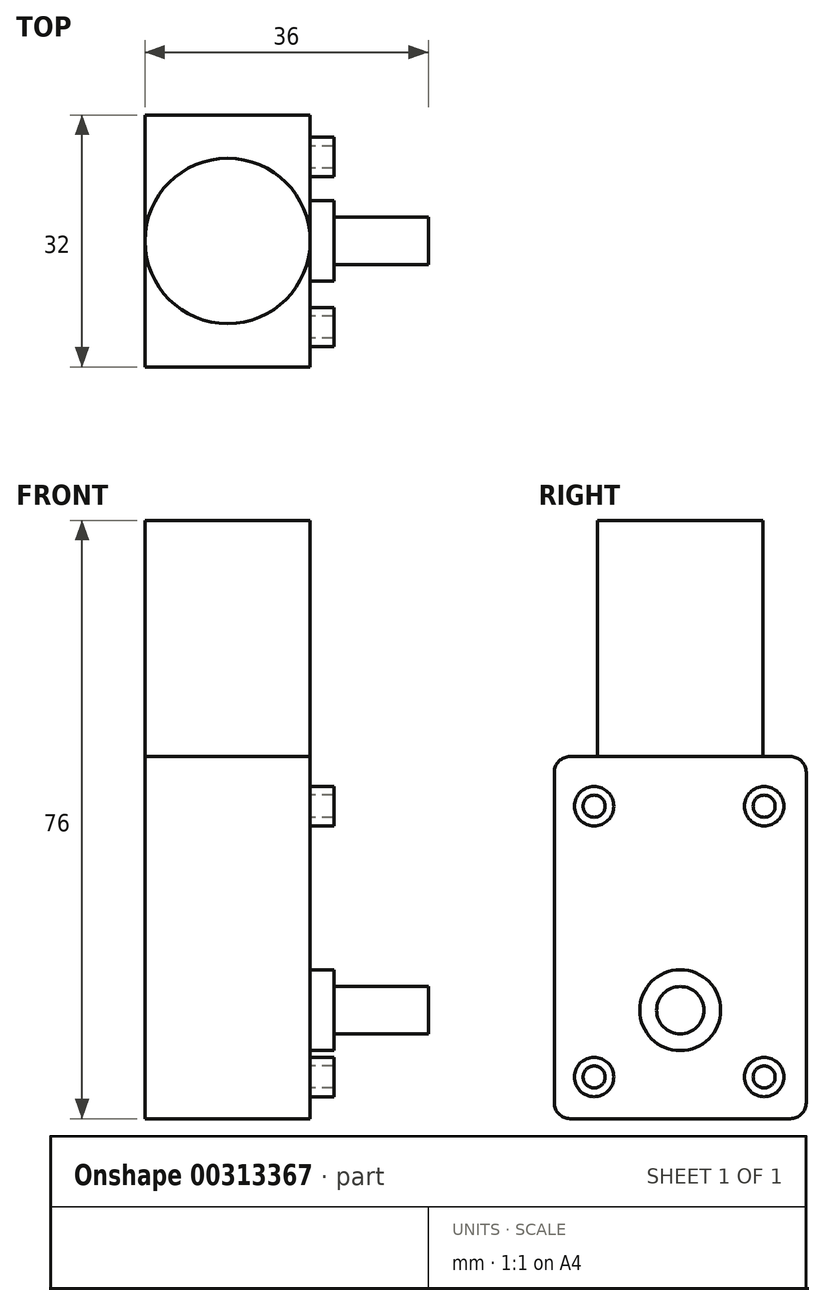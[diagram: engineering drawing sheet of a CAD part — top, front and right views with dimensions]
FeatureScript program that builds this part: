
annotation { "Feature Type Name" : "Feature", "Feature Type Description" : "" }
export const myFeature = defineFeature(function(context is Context, id is Id, definition is map)
    precondition{}
    {
        {
            var Q0;
            Q0=qCreatedBy(makeId("Front.planeOp"),FACE);
            var sketch = newSketch(context, id + "F0", { "sketchPlane" : qUnion([Q0])});
            skLineSegment(sketch, "E0.bottom", {"start": v(-20.31, 46) * mm, "end": v(0.69, 46) * mm});
            skLineSegment(sketch, "E0.top", {"start": v(-20.31, 0) * mm, "end": v(0.69, 0) * mm});
            skLineSegment(sketch, "E0.left", {"start": v(-20.31, 46) * mm, "end": v(-20.31, 0) * mm});
            skLineSegment(sketch, "E0.right", {"start": v(0.69, 46) * mm, "end": v(0.69, 0) * mm});
            skSolve(sketch);
        }
        {
            var Q0;
            Q0=makeQuery(id+"F0.imprint","IMPRINT",FACE,{"disambiguationData":[TD([[makeQuery(id+"F0.imprint","IMPRINT",EDGE,{"derivedFrom":sQuery(id+"F0.wireOp",EDGE,"E0.bottom")}),-1.0]])]});
            extrude(context, id + "F1", {"entities" : qUnion([Q0]), "endBound" : BoundingType.SYMMETRIC, "depth" : 32 * mm});
        }
        {
            var Q0;
            Q0=makeQuery(id+"F1.opExtrude","SWEPT_FACE",FACE,{"disambiguationData":[OSD([sQuery(id+"F0.wireOp",EDGE,"E0.right")])]});
            var sketch = newSketch(context, id + "F2", { "sketchPlane" : qUnion([Q0])});
            skCircle(sketch, "E1", {"center": v(-10.94, 39.7) * mm, "radius": 2.5 * mm});
            skCircle(sketch, "E2", {"center": v(-10.94, 39.7) * mm, "radius": 1.4 * mm});
            skCircle(sketch, "E3.1.0.0", {"center": v(10.66, 39.7) * mm, "radius": 1.4 * mm});
            skCircle(sketch, "E3.1.0.1", {"center": v(10.66, 39.7) * mm, "radius": 2.5 * mm});
            skLineSegment(sketch, "E3.direction1", {"start": v(-10.94, 39.7) * mm, "end": v(10.66, 39.7) * mm, "construction": true});
            skCircle(sketch, "E4.1.0.0", {"center": v(10.66, 5.3) * mm, "radius": 2.5 * mm});
            skCircle(sketch, "E4.1.0.1", {"center": v(10.66, 5.3) * mm, "radius": 1.4 * mm});
            skLineSegment(sketch, "E4.1.0.2", {"start": v(-10.94, 5.3) * mm, "end": v(10.66, 5.3) * mm, "construction": true});
            skCircle(sketch, "E4.1.0.3", {"center": v(-10.94, 5.3) * mm, "radius": 1.4 * mm});
            skCircle(sketch, "E4.1.0.4", {"center": v(-10.94, 5.3) * mm, "radius": 2.5 * mm});
            skLineSegment(sketch, "E4.direction1", {"start": v(-10.94, 39.7) * mm, "end": v(-10.94, 5.3) * mm, "construction": true});
            skCircle(sketch, "E5", {"center": v(0, 13.78) * mm, "radius": 5.13 * mm});
            skCircle(sketch, "E6", {"center": v(0, 13.78) * mm, "radius": 3 * mm});
            skSolve(sketch);
        }
        {
            var Q0;
            Q0=makeQuery(id+"F2.imprint","IMPRINT",FACE,{"disambiguationData":[TD([[makeQuery(id+"F2.imprint","IMPRINT",EDGE,{"derivedFrom":sQuery(id+"F2.wireOp",EDGE,"E6")}),1.0]])]});
            extrude(context, id + "F3", {"entities" : qUnion([Q0]), "operationType" : NewBodyOperationType.ADD, "depth" : 15 * mm});
        }
        {
            var Q0;
            Q0=makeQuery(id+"F2.imprint","IMPRINT",FACE,{"disambiguationData":[TD([[makeQuery(id+"F2.imprint","IMPRINT",EDGE,{"derivedFrom":sQuery(id+"F2.wireOp",EDGE,"E1")}),1.0]])]});
            var Q1;
            Q1=makeQuery(id+"F2.imprint","IMPRINT",FACE,{"disambiguationData":[TD([[makeQuery(id+"F2.imprint","IMPRINT",EDGE,{"derivedFrom":sQuery(id+"F2.wireOp",EDGE,"E4.1.0.3")}),-1.0]])]});
            var Q2;
            Q2=makeQuery(id+"F2.imprint","IMPRINT",FACE,{"disambiguationData":[TD([[makeQuery(id+"F2.imprint","IMPRINT",EDGE,{"derivedFrom":sQuery(id+"F2.wireOp",EDGE,"E4.1.0.0")}),1.0]])]});
            var Q3;
            Q3=makeQuery(id+"F2.imprint","IMPRINT",FACE,{"disambiguationData":[TD([[makeQuery(id+"F2.imprint","IMPRINT",EDGE,{"derivedFrom":sQuery(id+"F2.wireOp",EDGE,"E3.1.0.0")}),-1.0]])]});
            var Q4;
            Q4=makeQuery(id+"F2.imprint","IMPRINT",FACE,{"disambiguationData":[TD([[makeQuery(id+"F2.imprint","IMPRINT",EDGE,{"derivedFrom":sQuery(id+"F2.wireOp",EDGE,"E5")}),1.0]])]});
            extrude(context, id + "F4", {"entities" : qUnion([Q0, Q1, Q2, Q3, Q4]), "operationType" : NewBodyOperationType.ADD, "depth" : 3 * mm});
        }
        {
            var Q0;
            Q0=makeQuery(id+"F4.opExtrude","CAP_EDGE",EDGE,{"disambiguationData":[OSD([sQuery(id+"F2.wireOp",EDGE,"E1")])],"isStart":true});
            var Q1;
            Q1=makeQuery(id+"F4.opExtrude","CAP_EDGE",EDGE,{"disambiguationData":[OSD([sQuery(id+"F2.wireOp",EDGE,"E4.1.0.4")])],"isStart":true});
            var Q2;
            Q2=makeQuery(id+"F4.opExtrude","CAP_EDGE",EDGE,{"disambiguationData":[OSD([sQuery(id+"F2.wireOp",EDGE,"E5")])],"isStart":true});
            var Q3;
            Q3=makeQuery(id+"F4.opExtrude","CAP_EDGE",EDGE,{"disambiguationData":[OSD([sQuery(id+"F2.wireOp",EDGE,"E4.1.0.0")])],"isStart":true});
            var Q4;
            Q4=makeQuery(id+"F4.opExtrude","CAP_EDGE",EDGE,{"disambiguationData":[OSD([sQuery(id+"F2.wireOp",EDGE,"E3.1.0.1")])],"isStart":true});
            var Q5;
            Q5=makeQuery(id+"F1.opExtrude","CAP_EDGE",EDGE,{"disambiguationData":[OSD([sQuery(id+"F0.wireOp",EDGE,"E0.bottom")])],"isStart":false});
            var Q6;
            Q6=makeQuery(id+"F1.opExtrude","CAP_EDGE",EDGE,{"disambiguationData":[OSD([sQuery(id+"F0.wireOp",EDGE,"E0.top")])],"isStart":false});
            var Q7;
            Q7=makeQuery(id+"F1.opExtrude","CAP_EDGE",EDGE,{"disambiguationData":[OSD([sQuery(id+"F0.wireOp",EDGE,"E0.top")])],"isStart":true});
            var Q8;
            Q8=makeQuery(id+"F1.opExtrude","CAP_EDGE",EDGE,{"disambiguationData":[OSD([sQuery(id+"F0.wireOp",EDGE,"E0.bottom")])],"isStart":true});
            fillet(context, id + "F5", {"entities" : qUnion([Q0, Q1, Q2, Q3, Q4, Q5, Q6, Q7, Q8]), "radius" : 2 * mm, "tangentPropagation" : true, "allowEdgeOverflow" : false});
        }
        {
            var Q0;
            Q0=makeQuery(id+"F1.opExtrude","SWEPT_FACE",FACE,{"disambiguationData":[OSD([sQuery(id+"F0.wireOp",EDGE,"E0.bottom")])]});
            var sketch = newSketch(context, id + "F6", { "sketchPlane" : qUnion([Q0])});
            skCircle(sketch, "E7", {"center": v(-9.81, 0) * mm, "radius": 10.5 * mm});
            skPoint(sketch, "E7.centerSnap0", {"position": v(0.69, 0) * mm});
            skSolve(sketch);
        }
        {
            var Q0;
            {var subQ0=sQuery(id+"F6.wireOp",EDGE,"E7");var subQ1=sQuery(id+"F0.wireOp",EDGE,"E0.bottom");var subQ2=makeQuery(id+"F6.imprint","INTERSECT",VERTEX,{"derivedFrom":[makeQuery(id+"F1.opExtrude","SWEPT_EDGE",EDGE,{"disambiguationData":[OSD([subQ1,sQuery(id+"F0.wireOp",EDGE,"E0.left")])]}),subQ0]});Q0=makeQuery(id+"F6.imprint","IMPRINT",FACE,{"disambiguationData":[TD([[makeQuery(id+"F6.imprint","IMPRINT",EDGE,{"disambiguationData":[TD([[subQ2,1.0]])],"derivedFrom":subQ0}),1.0]])]});}
            extrude(context, id + "F7", {"entities" : qUnion([Q0]), "operationType" : NewBodyOperationType.ADD, "depth" : 30 * mm});
        }
    });
